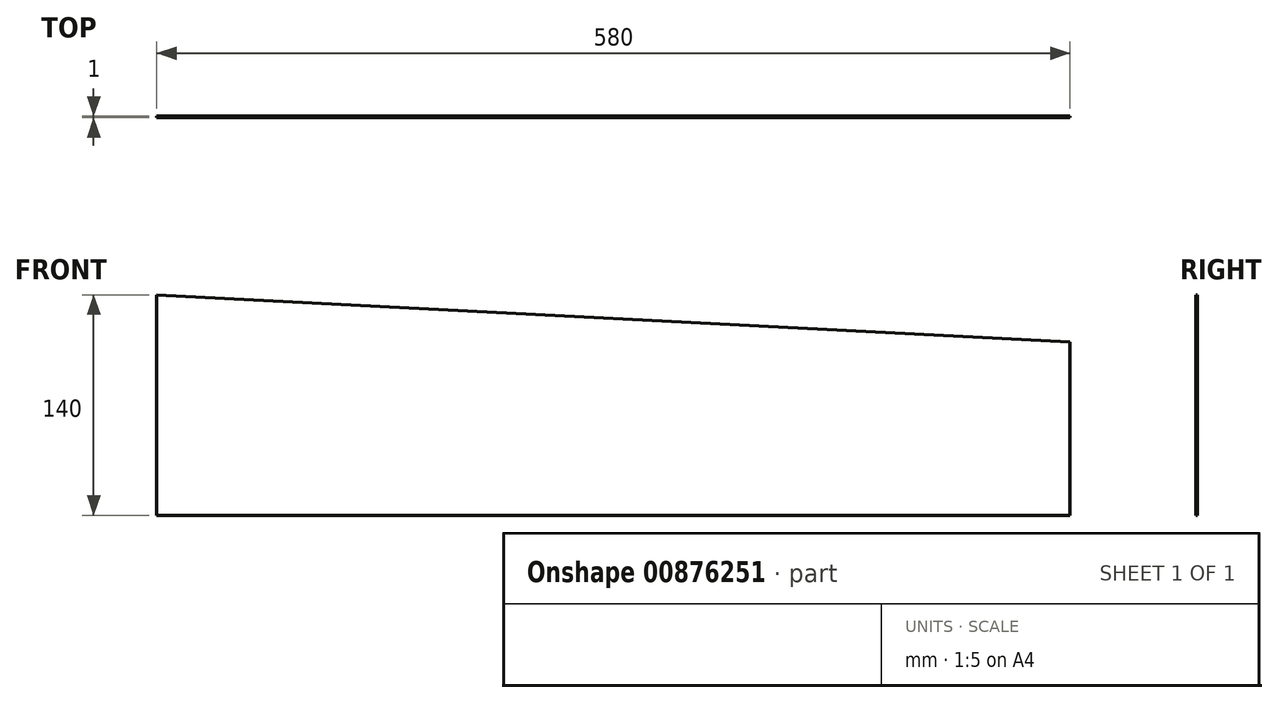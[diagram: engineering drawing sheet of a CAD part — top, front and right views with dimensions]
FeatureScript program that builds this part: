
annotation { "Feature Type Name" : "Feature", "Feature Type Description" : "" }
export const myFeature = defineFeature(function(context is Context, id is Id, definition is map)
    precondition{}
    {
        {
            var Q0;
            Q0=qCreatedBy(makeId("Front.planeOp"),FACE);
            var sketch = newSketch(context, id + "F0", { "sketchPlane" : qUnion([Q0])});
            skLineSegment(sketch, "E0", {"start": v(0, 0) * mm, "end": v(0, 140) * mm});
            skLineSegment(sketch, "E1", {"start": v(0, 140) * mm, "end": v(580, 110) * mm});
            skLineSegment(sketch, "E2", {"start": v(580, 110) * mm, "end": v(580, 0) * mm});
            skLineSegment(sketch, "E3", {"start": v(580, 0) * mm, "end": v(0, 0) * mm});
            skSolve(sketch);
        }
        {
            var Q0;
            Q0=makeQuery(id+"F0.imprint","IMPRINT",FACE,{"disambiguationData":[TD([[makeQuery(id+"F0.imprint","IMPRINT",EDGE,{"derivedFrom":sQuery(id+"F0.wireOp",EDGE,"E0")}),-1.0]])]});
            extrude(context, id + "F1", {"entities" : qUnion([Q0]), "depth" : 1 * mm, "offsetDistance" : 25.4 * mm});
        }
    });
